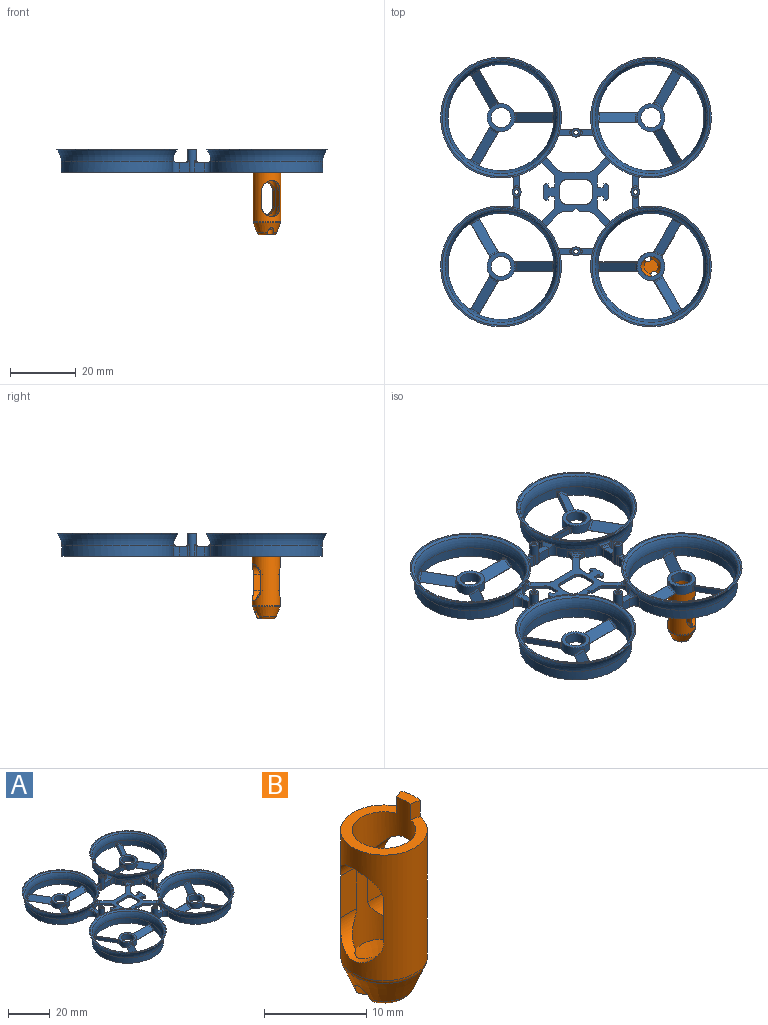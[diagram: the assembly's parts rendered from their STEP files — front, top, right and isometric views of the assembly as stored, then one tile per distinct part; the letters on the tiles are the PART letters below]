
ASSEMBLY  parts=2 mates=1
PART A: 307 faces, bbox 86.5x86.2x9.8 mm
  f0: cylinder r=17mm len=8.72mm, axis (0,0,-1), area 26.2mm2, adj f4,f62,f158,f159,f187,f194,f279
  f1: cylinder r=17mm len=8.72mm, axis (0,0,-1), area 26.2mm2, adj f4,f77,f162,f163,f185,f197,f282
  f2: cylinder r=17mm len=33.99mm, axis (0,0,-1), area 259.6mm2, adj f4,f80,f189,f196
  f3: cylinder r=17mm len=8.72mm, axis (0,0,-1), area 26.2mm2, adj f4,f59,f166,f167,f191,f200,f292
  f4: plane 79.71x79.36mm, normal (0,0,-1), area 1160.2mm2, adj f0,f1,f2,f3,f13,f14,f15,f16
  f5: plane 11.58x7.59mm, normal (0,0,1), area 2.2mm2, adj f33,f35,f43,f74,f229,f230,f257,f258
  f6: plane 12.55x1.9mm, normal (0,0,1), area 2.2mm2, adj f33,f35,f40,f73,f231,f232,f259,f260
  f7: plane 11.25x7.41mm, normal (0,0,1), area 0.3mm2, adj f30,f32,f38,f66,f245,f246,f261,f262
  f8: plane 12.55x1.76mm, normal (0,0,1), area 0.3mm2, adj f30,f32,f48,f68,f241,f242,f267,f268
  f9: plane 12.55x1.76mm, normal (0,0,1), area 0.3mm2, adj f24,f26,f47,f63,f251,f252,f271,f272
  f10: plane 11.25x7.41mm, normal (0,0,1), area 0.3mm2, adj f24,f26,f29,f65,f247,f248,f269,f270
  f11: plane 12.55x1.76mm, normal (0,0,1), area 0.3mm2, adj f21,f23,f45,f71,f235,f236,f253,f254
  f12: plane 11.49x7.48mm, normal (0,0,1), area 0.3mm2, adj f21,f23,f27,f70,f237,f238,f273,f274
  f13: cylinder r=17mm len=33.99mm, axis (0,0,-1), area 259.6mm2, adj f4,f59,f192,f199
  f14: cylinder r=17mm len=33.99mm, axis (0,0,-1), area 259.6mm2, adj f4,f77,f186,f198
  f15: cylinder r=17mm len=8.72mm, axis (0,0,-1), area 26.2mm2, adj f4,f80,f170,f171,f190,f195,f289
  f16: cylinder r=17mm len=33.99mm, axis (0,0,-1), area 259.6mm2, adj f4,f62,f188,f193
  f17: plane 11.49x7.48mm, normal (0,0,1), area 0.3mm2, adj f30,f32,f44,f67,f243,f244,f255,f256
  f18: plane 11.25x7.41mm, normal (0,0,1), area 0.3mm2, adj f24,f26,f36,f64,f249,f250,f263,f264
  f19: plane 11.25x7.41mm, normal (0,0,1), area 0.3mm2, adj f21,f23,f56,f69,f239,f240,f275,f276
  f20: plane 11.31x7.56mm, normal (0,0,1), area 2.2mm2, adj f33,f35,f49,f72,f233,f234,f265,f266
  f21: cylinder r=4.25mm len=8.5mm, axis (0,0,-1), area 64.3mm2, adj f4,f11,f12,f19,f22,f28,f55,f177
  f22: plane 12.26x0.79mm, normal (0,-1,0), area 0.7mm2, adj f4,f21,f23,f71,f235,f236
  f23: cylinder r=16.2mm len=32.39mm, axis (0,0,-1), area 300.6mm2, adj f4,f11,f12,f19,f22,f28,f55,f57
  f24: cylinder r=4.25mm len=8.5mm, axis (0,0,-1), area 64.3mm2, adj f4,f9,f10,f18,f25,f37,f46,f178
  f25: plane 10.64x6.19mm, normal (-0.87,0.5,0), area 0.7mm2, adj f4,f24,f26,f64,f249,f250
  f26: cylinder r=16.2mm len=32.39mm, axis (0,0,-1), area 300.6mm2, adj f4,f9,f10,f18,f25,f37,f46,f75
  f27: plane 9.75x5.63mm, normal (-0.87,-0.5,0), area 22.5mm2, adj f4,f12,f273,f274
  f28: plane 10.64x6.19mm, normal (-0.87,0.5,0), area 0.7mm2, adj f4,f21,f23,f69,f239,f240
  f29: plane 9.75x5.63mm, normal (0.87,0.5,0), area 22.5mm2, adj f4,f10,f269,f270
  f30: cylinder r=4.25mm len=8.5mm, axis (0,0,-1), area 64.3mm2, adj f4,f7,f8,f17,f31,f39,f50,f179
  f31: plane 10.64x6.19mm, normal (-0.87,-0.5,0), area 0.7mm2, adj f4,f30,f32,f67,f243,f244
  f32: cylinder r=16.2mm len=32.39mm, axis (0,0,-1), area 300.6mm2, adj f4,f7,f8,f17,f31,f39,f50,f60
  f33: cylinder r=16.2mm len=32.39mm, axis (0,0,-1), area 300mm2, adj f4,f5,f6,f20,f34,f41,f42,f78
  f34: plane 12.26x0.89mm, normal (0,-1,0), area 2mm2, adj f4,f33,f35,f73,f231,f232
  f35: cylinder r=4.25mm len=8.5mm, axis (0,0,-1), area 63.8mm2, adj f4,f5,f6,f20,f34,f41,f42,f180
  f36: plane 9.75x5.63mm, normal (0.87,-0.5,0), area 22.5mm2, adj f4,f18,f263,f264
  f37: plane 12.26x0.79mm, normal (0,-1,0), area 0.7mm2, adj f4,f24,f26,f63,f251,f252
  f38: plane 9.75x5.63mm, normal (-0.87,0.5,0), area 22.5mm2, adj f4,f7,f261,f262
  f39: plane 12.26x0.79mm, normal (0,1,0), area 0.7mm2, adj f4,f30,f32,f68,f241,f242
  f40: plane 11.26x2mm, normal (0,1,0), area 22.5mm2, adj f4,f6,f259,f260
  f41: plane 10.64x6.19mm, normal (-0.87,0.5,0), area 2mm2, adj f4,f33,f35,f74,f229,f230
  f42: plane 10.64x6.19mm, normal (0.87,0.5,0), area 2mm2, adj f4,f33,f35,f72,f233,f234
  f43: plane 9.75x5.63mm, normal (0.87,-0.5,0), area 22.5mm2, adj f4,f5,f257,f258
  f44: plane 9.75x5.63mm, normal (0.87,0.5,0), area 22.5mm2, adj f4,f17,f255,f256
  f45: plane 11.26x2mm, normal (0,1,0), area 22.5mm2, adj f4,f11,f253,f254
  f46: plane 10.64x6.19mm, normal (-0.87,-0.5,0), area 0.7mm2, adj f4,f24,f26,f65,f247,f248
  f47: plane 11.26x2mm, normal (0,1,0), area 22.5mm2, adj f4,f9,f271,f272
  f48: plane 11.26x2mm, normal (0,-1,0), area 22.5mm2, adj f4,f8,f267,f268
  f49: plane 9.75x5.63mm, normal (-0.87,-0.5,0), area 22.5mm2, adj f4,f20,f265,f266
  f50: plane 10.64x6.19mm, normal (0.87,-0.5,0), area 0.7mm2, adj f4,f30,f32,f66,f245,f246
  f51: cylinder r=3.05mm len=6.1mm, axis (0,0,-1), area 57.5mm2, adj f4,f178
  f52: cylinder r=3.05mm len=6.1mm, axis (0,0,-1), area 57.5mm2, adj f4,f179
  f53: cylinder r=3.05mm len=6.1mm, axis (0,0,-1), area 57.5mm2, adj f4,f180
  f54: cylinder r=3.05mm len=6.1mm, axis (0,0,-1), area 57.5mm2, adj f4,f177
  f55: plane 10.64x6.19mm, normal (0.87,0.5,0), area 0.7mm2, adj f4,f21,f23,f70,f237,f238
  f56: plane 9.75x5.63mm, normal (0.87,-0.5,0), area 22.5mm2, adj f4,f19,f275,f276
  f57: torus R=22.96mm, axis (0,0,1), area 366.2mm2, adj f23,f84
  f58: plane 36.83x36.83mm, normal (0,0,1), area 51.6mm2, adj f59,f84
  f59: torus R=23mm, axis (0,0,1), area 449.2mm2, adj f3,f13,f58,f191,f192,f199,f200,f293
  f60: torus R=22.96mm, axis (0,0,1), area 366.2mm2, adj f32,f83
  f61: plane 36.83x36.83mm, normal (0,0,1), area 51.6mm2, adj f62,f83
  f62: torus R=23mm, axis (0,0,1), area 451.7mm2, adj f0,f16,f61,f187,f188,f193,f194,f214
  f63: plane 11.29x3mm, normal (0,-0.54,0.84), area 39.4mm2, adj f9,f37,f251,f252
  f64: plane 11.23x8.1mm, normal (-0.47,0.27,0.84), area 39.4mm2, adj f18,f25,f249,f250
  f65: plane 11.23x8.1mm, normal (-0.47,-0.27,0.84), area 39.4mm2, adj f10,f46,f247,f248
  f66: plane 11.23x8.1mm, normal (0.47,-0.27,0.84), area 39.4mm2, adj f7,f50,f245,f246
  f67: plane 11.03x8.22mm, normal (-0.47,-0.27,0.84), area 39.4mm2, adj f17,f31,f243,f244
  f68: plane 11.29x3mm, normal (0,0.54,0.84), area 39.4mm2, adj f8,f39,f241,f242
  f69: plane 11.23x8.1mm, normal (-0.47,0.27,0.84), area 39.4mm2, adj f19,f28,f239,f240
  f70: plane 11.03x8.22mm, normal (0.47,0.27,0.84), area 39.4mm2, adj f12,f55,f237,f238
  f71: plane 11.29x3mm, normal (0,-0.54,0.84), area 39.4mm2, adj f11,f22,f235,f236
  f72: plane 11.17x7.95mm, normal (0.47,0.27,0.84), area 37.3mm2, adj f20,f42,f233,f234
  f73: plane 11.29x2.85mm, normal (0,-0.54,0.84), area 37.3mm2, adj f6,f34,f231,f232
  f74: plane 10.92x8.09mm, normal (-0.47,0.27,0.84), area 37.3mm2, adj f5,f41,f229,f230
  f75: torus R=22.96mm, axis (0,0,1), area 366.2mm2, adj f26,f82
  f76: plane 36.83x36.83mm, normal (0,0,1), area 51.6mm2, adj f77,f82
  f77: torus R=23mm, axis (0,0,1), area 451.7mm2, adj f1,f14,f76,f185,f186,f197,f198,f213
  f78: torus R=22.96mm, axis (0,0,1), area 366.2mm2, adj f33,f81
  f79: plane 36.83x36.83mm, normal (0,0,1), area 51.6mm2, adj f80,f81
  f80: torus R=23mm, axis (0,0,1), area 451.7mm2, adj f2,f15,f79,f189,f190,f195,f196,f216
  f81: torus R=17.96mm, axis (0,0,-1), area 115.2mm2, adj f78,f79
  f82: torus R=17.96mm, axis (0,0,-1), area 115.2mm2, adj f75,f76
  f83: torus R=17.96mm, axis (0,0,-1), area 115.2mm2, adj f60,f61
  f84: torus R=17.96mm, axis (0,0,-1), area 115.2mm2, adj f57,f58
  f85: cylinder r=1.35mm len=7mm, axis (0,0,-1), area 40.1mm2, adj f4,f86,f207,f208,f295,f296,f297,f298
  f86: plane 2.7x2.7mm, normal (0,0,1), area 4.4mm2, adj f85,f154
  f87: cylinder r=1.35mm len=7mm, axis (0,0,-1), area 40.1mm2, adj f4,f88,f201,f202,f303,f304,f305,f306
  f88: plane 2.7x2.7mm, normal (0,0,1), area 4.4mm2, adj f87,f153
  f89: cylinder r=1.35mm len=7mm, axis (0,0,-1), area 41.9mm2, adj f4,f90,f107,f109,f203,f204,f299,f300
  f90: plane 2.7x2.7mm, normal (0,0,1), area 4.4mm2, adj f89,f156
  f91: cylinder r=1.35mm len=7mm, axis (0,0,-1), area 41.9mm2, adj f4,f92,f101,f103,f205,f206,f301,f302
  f92: plane 2.7x2.7mm, normal (0,0,1), area 4.4mm2, adj f91,f155
  f93: plane 4.21x2.44mm, normal (0,0,1), area 7.6mm2, adj f94,f95,f187,f188,f208,f214
  f94: plane 3.08x2.71mm, normal (0,1,0), area 8.1mm2, adj f4,f93,f188,f208,f298
  f95: plane 4.22x3.08mm, normal (0,-1,0), area 12.6mm2, adj f4,f93,f187,f208,f296
  f96: plane 4.21x2.44mm, normal (0,0,1), area 7.6mm2, adj f97,f98,f185,f186,f207,f213
  f97: plane 3.08x2.71mm, normal (0,1,0), area 8.1mm2, adj f4,f96,f186,f207,f297
  f98: plane 4.22x3.08mm, normal (0,-1,0), area 12.6mm2, adj f4,f96,f185,f207,f295
  f99: plane 4.09x2.45mm, normal (0,0,1), area 7.4mm2, adj f100,f101,f195,f196,f206,f216
  f100: plane 4.13x3.08mm, normal (-1,0,0), area 12.4mm2, adj f4,f99,f195,f206,f302
  f101: plane 3.59x2.96mm, normal (1,0,0), area 8.7mm2, adj f4,f91,f99,f196,f206
  f102: plane 3.65x2.19mm, normal (0,0,1), area 6.4mm2, adj f103,f104,f193,f205,f278
  f103: plane 3.59x2.96mm, normal (1,0,0), area 8.7mm2, adj f4,f91,f102,f193,f205
  f104: plane 4.13x3.08mm, normal (-1,0,0), area 12.4mm2, adj f4,f102,f194,f205,f278,f301
  f105: plane 3.76x2.18mm, normal (0,0,1), area 6.6mm2, adj f106,f107,f189,f204,f288
  f106: plane 4.22x3.08mm, normal (0,1,0), area 12.6mm2, adj f4,f105,f190,f204,f288,f299
  f107: plane 3.59x3.12mm, normal (0,-1,0), area 9.1mm2, adj f4,f89,f105,f189,f204
  f108: plane 3.76x2.18mm, normal (0,0,1), area 6.6mm2, adj f109,f110,f192,f203,f291
  f109: plane 3.59x3.12mm, normal (0,-1,0), area 9.1mm2, adj f4,f89,f108,f192,f203
  f110: plane 4.22x3.08mm, normal (0,1,0), area 12.6mm2, adj f4,f108,f191,f203,f291,f300
  f111: plane 3.65x2.19mm, normal (0,0,1), area 6.4mm2, adj f112,f113,f199,f202,f283
  f112: plane 3.08x2.55mm, normal (-1,0,0), area 7.6mm2, adj f4,f111,f199,f202,f306
  f113: plane 4.13x3.08mm, normal (1,0,0), area 12.4mm2, adj f4,f111,f200,f202,f283,f303
  f114: plane 3.65x2.19mm, normal (0,0,1), area 6.4mm2, adj f115,f116,f198,f201,f277
  f115: plane 4.13x3.08mm, normal (1,0,0), area 12.4mm2, adj f4,f114,f197,f201,f277,f304
  f116: plane 3.08x2.55mm, normal (-1,0,0), area 7.6mm2, adj f4,f114,f198,f201,f305
  f117: plane 5.8x1mm, normal (0,-1,0), area 5.8mm2, adj f4,f152,f173,f176
  f118: plane 3.5x1mm, normal (-1,0,0), area 3.5mm2, adj f4,f152,f173,f174
  f119: plane 5.8x1mm, normal (0,1,0), area 5.8mm2, adj f4,f152,f174,f175
  f120: plane 2.41x1mm, normal (1,0,0), area 2.4mm2, adj f4,f152,f157,f228
  f121: plane 3.21x3.19mm, normal (0.7,-0.71,0), area 4.5mm2, adj f4,f152,f157,f158
  f122: plane 3.63x3.6mm, normal (-0.7,0.71,0), area 5.1mm2, adj f4,f152,f159,f160
  f123: plane 7.6x1mm, normal (0,1,0), area 7.6mm2, adj f4,f152,f160,f161
  f124: plane 3.63x3.6mm, normal (0.7,0.71,0), area 5.1mm2, adj f4,f152,f161,f162
  f125: plane 3.21x3.19mm, normal (-0.7,-0.71,0), area 4.5mm2, adj f4,f152,f163,f164
  f126: plane 2.41x1mm, normal (-1,0,0), area 2.4mm2, adj f4,f152,f164,f221
  f127: plane 1x1mm, normal (0,1,0), area 1mm2, adj f4,f152,f221,f222
  f128: plane 1x0.75mm, normal (1,0,0), area 0.8mm2, adj f4,f129,f152,f222
  f129: plane 1x0.5mm, normal (0,1,0), area 0.5mm2, adj f4,f128,f152,f181
  f130: plane 3x1mm, normal (-1,0,0), area 3mm2, adj f4,f152,f181,f182
  f131: plane 1x0.5mm, normal (0,-1,0), area 0.5mm2, adj f4,f132,f152,f182
  f132: plane 1x0.75mm, normal (1,0,0), area 0.8mm2, adj f4,f131,f152,f223
  f133: plane 1x1mm, normal (0,-1,0), area 1mm2, adj f4,f152,f223,f224
  f134: plane 2.41x1mm, normal (-1,0,0), area 2.4mm2, adj f4,f152,f165,f224
  f135: plane 3.21x3.19mm, normal (-0.7,0.71,0), area 4.5mm2, adj f4,f152,f165,f166
  f136: plane 3.63x3.6mm, normal (0.7,-0.71,0), area 5.1mm2, adj f4,f152,f167,f168
  f137: plane 2.81x1mm, normal (0,-1,0), area 2.8mm2, adj f4,f138,f152,f168
  f138: plane 1x1mm, normal (0.71,-0.7,0), area 1.4mm2, adj f4,f137,f139,f152
  f139: plane 1.01x1mm, normal (-0.7,-0.71,0), area 1.4mm2, adj f4,f138,f140,f152
  f140: plane 2.79x1mm, normal (0,-1,0), area 2.8mm2, adj f4,f139,f152,f169
  f141: plane 3.63x3.6mm, normal (-0.7,-0.71,0), area 5.1mm2, adj f4,f152,f169,f170
  f142: plane 3.21x3.19mm, normal (0.7,0.71,0), area 4.5mm2, adj f4,f152,f171,f172
  f143: plane 2.41x1mm, normal (1,0,0), area 2.4mm2, adj f4,f152,f172,f225
  f144: plane 1x1mm, normal (0,-1,0), area 1mm2, adj f4,f152,f225,f226
  f145: plane 1x0.75mm, normal (-1,0,0), area 0.8mm2, adj f4,f146,f152,f226
  f146: plane 1x0.5mm, normal (0,-1,0), area 0.5mm2, adj f4,f145,f152,f183
  f147: plane 3x1mm, normal (1,0,0), area 3mm2, adj f4,f152,f183,f184
  f148: plane 1x0.5mm, normal (0,1,0), area 0.5mm2, adj f4,f149,f152,f184
  f149: plane 1x0.75mm, normal (-1,0,0), area 0.8mm2, adj f4,f148,f152,f227
  f150: plane 1x1mm, normal (0,1,0), area 1mm2, adj f4,f152,f227,f228
  f151: plane 3.5x1mm, normal (1,0,0), area 3.5mm2, adj f4,f152,f175,f176
  f152: plane 21.09x20.95mm, normal (0,0,1), area 153.4mm2, adj f117,f118,f119,f120,f121,f122,f123,f124
  f153: cylinder r=0.65mm len=7mm, axis (0,0,1), area 28.6mm2, adj f4,f88
  f154: cylinder r=0.65mm len=7mm, axis (0,0,1), area 28.6mm2, adj f4,f86
  f155: cylinder r=0.65mm len=7mm, axis (0,0,1), area 28.6mm2, adj f4,f92
  f156: cylinder r=0.65mm len=7mm, axis (0,0,1), area 28.6mm2, adj f4,f90
  f157: cylinder r=2mm len=1.42mm, axis (0,0,-1), area 1.6mm2, adj f4,f120,f121,f152
  f158: cylinder r=2mm len=2.59mm, axis (0,0,-1), area 4.4mm2, adj f0,f4,f121,f152,f220,f279,f287
  f159: cylinder r=2mm len=2.59mm, axis (0,0,-1), area 4.4mm2, adj f0,f4,f122,f152,f220,f279,f287
  f160: cylinder r=2mm len=1.41mm, axis (0,0,1), area 1.6mm2, adj f4,f122,f123,f152
  f161: cylinder r=2mm len=1.41mm, axis (0,0,1), area 1.6mm2, adj f4,f123,f124,f152
  f162: cylinder r=2mm len=2.59mm, axis (0,0,-1), area 4.4mm2, adj f1,f4,f124,f152,f219,f282,f286
  f163: cylinder r=2mm len=2.59mm, axis (0,0,-1), area 4.4mm2, adj f1,f4,f125,f152,f219,f282,f286
  f164: cylinder r=2mm len=1.42mm, axis (0,0,1), area 1.6mm2, adj f4,f125,f126,f152
  f165: cylinder r=2mm len=1.42mm, axis (0,0,-1), area 1.6mm2, adj f4,f134,f135,f152
  f166: cylinder r=2mm len=2.59mm, axis (0,0,-1), area 4.4mm2, adj f3,f4,f135,f152,f215,f285,f292
  f167: cylinder r=2mm len=2.59mm, axis (0,0,-1), area 4.4mm2, adj f3,f4,f136,f152,f215,f285,f292
  f168: cylinder r=2mm len=1.41mm, axis (0,0,1), area 1.6mm2, adj f4,f136,f137,f152
  f169: cylinder r=2mm len=1.41mm, axis (0,0,1), area 1.6mm2, adj f4,f140,f141,f152
  f170: cylinder r=2mm len=2.59mm, axis (0,0,-1), area 4.4mm2, adj f4,f15,f141,f152,f211,f284,f289
  f171: cylinder r=2mm len=2.59mm, axis (0,0,-1), area 4.4mm2, adj f4,f15,f142,f152,f211,f284,f289
  f172: cylinder r=2mm len=1.42mm, axis (0,0,1), area 1.6mm2, adj f4,f142,f143,f152
  f173: cylinder r=2mm len=2mm, axis (0,0,1), area 3.1mm2, adj f4,f117,f118,f152
  f174: cylinder r=2mm len=2mm, axis (0,0,-1), area 3.1mm2, adj f4,f118,f119,f152
  f175: cylinder r=2mm len=2mm, axis (0,0,1), area 3.1mm2, adj f4,f119,f151,f152
  f176: cylinder r=2mm len=2mm, axis (0,0,-1), area 3.1mm2, adj f4,f117,f151,f152
  f177: plane 8.5x8.5mm, normal (0,0,1), area 27.5mm2, adj f21,f54
  f178: plane 8.5x8.5mm, normal (0,0,1), area 27.5mm2, adj f24,f51
  f179: plane 8.5x8.5mm, normal (0,0,1), area 27.5mm2, adj f30,f52
  f180: plane 8.5x8.5mm, normal (0,0,1), area 27.5mm2, adj f35,f53
  f181: cylinder r=1mm len=1mm, axis (0,0,-1), area 1.6mm2, adj f4,f129,f130,f152
  f182: cylinder r=1mm len=1mm, axis (0,0,-1), area 1.6mm2, adj f4,f130,f131,f152
  f183: cylinder r=1mm len=1mm, axis (0,0,-1), area 1.6mm2, adj f4,f146,f147,f152
  f184: cylinder r=1mm len=1mm, axis (0,0,-1), area 1.6mm2, adj f4,f147,f148,f152
  f185: cylinder r=2mm len=3.94mm, axis (0,0,-1), area 7.9mm2, adj f1,f4,f77,f96,f98,f213
  f186: cylinder r=2mm len=3.94mm, axis (0,0,-1), area 10.9mm2, adj f4,f14,f77,f96,f97,f213
  f187: cylinder r=2mm len=3.94mm, axis (0,0,-1), area 7.9mm2, adj f0,f4,f62,f93,f95,f214
  f188: cylinder r=2mm len=3.94mm, axis (0,0,-1), area 10.9mm2, adj f4,f16,f62,f93,f94,f214
  f189: cylinder r=2mm len=4.51mm, axis (0,0,-1), area 11.2mm2, adj f2,f4,f80,f105,f107,f210,f288,f290
  f190: cylinder r=2mm len=4.51mm, axis (0,0,-1), area 8.2mm2, adj f4,f15,f80,f106,f210,f288,f290
  f191: cylinder r=2mm len=4.51mm, axis (0,0,-1), area 8.2mm2, adj f3,f4,f59,f110,f209,f291,f293
  f192: cylinder r=2mm len=4.51mm, axis (0,0,-1), area 11.2mm2, adj f4,f13,f59,f108,f109,f209,f291,f293
  f193: cylinder r=2mm len=4.51mm, axis (0,0,-1), area 11.3mm2, adj f4,f16,f62,f102,f103,f217,f278,f280
  f194: cylinder r=2mm len=4.51mm, axis (0,0,-1), area 8.2mm2, adj f0,f4,f62,f104,f217,f278,f280
  f195: cylinder r=2mm len=3.94mm, axis (0,0,-1), area 7.9mm2, adj f4,f15,f80,f99,f100,f216
  f196: cylinder r=2mm len=3.94mm, axis (0,0,-1), area 11mm2, adj f2,f4,f80,f99,f101,f216
  f197: cylinder r=2mm len=4.51mm, axis (0,0,-1), area 8.2mm2, adj f1,f4,f77,f115,f218,f277,f281
  f198: cylinder r=2mm len=4.51mm, axis (0,0,-1), area 11.3mm2, adj f4,f14,f77,f114,f116,f218,f277,f281
  f199: cylinder r=2mm len=4.51mm, axis (0,0,-1), area 11.3mm2, adj f4,f13,f59,f111,f112,f212,f283,f294
  f200: cylinder r=2mm len=4.51mm, axis (0,0,-1), area 8.2mm2, adj f3,f4,f59,f113,f212,f283,f294
  f201: torus R=1.85mm, axis (0,0,1), area 1.8mm2, adj f87,f114,f115,f116,f304,f305
  f202: torus R=1.85mm, axis (0,0,1), area 1.8mm2, adj f87,f111,f112,f113,f303,f306
  f203: torus R=1.85mm, axis (0,0,1), area 1.7mm2, adj f89,f108,f109,f110,f300
  f204: torus R=1.85mm, axis (0,0,1), area 1.7mm2, adj f89,f105,f106,f107,f299
  f205: torus R=1.85mm, axis (0,0,1), area 1.7mm2, adj f91,f102,f103,f104,f301
  f206: torus R=1.85mm, axis (0,0,1), area 1.7mm2, adj f91,f99,f100,f101,f302
  f207: torus R=1.85mm, axis (0,0,1), area 1.8mm2, adj f85,f96,f97,f98,f295,f297
  f208: torus R=1.85mm, axis (0,0,1), area 1.8mm2, adj f85,f93,f94,f95,f296,f298
  f209: cone r=17mm half-angle=45deg, axis (0,0,-1), area 1.2mm2, adj f191,f192,f291,f293
  f210: cone r=17mm half-angle=45deg, axis (0,0,-1), area 1.2mm2, adj f189,f190,f288,f290
  f211: cone r=17mm half-angle=45deg, axis (0,0,-1), area 1.8mm2, adj f170,f171,f284,f289
  f212: cone r=17mm half-angle=45deg, axis (0,0,-1), area 1.2mm2, adj f199,f200,f283,f294
  f213: cone r=18mm half-angle=45deg, axis (0,0,-1), area 4.8mm2, adj f77,f96,f185,f186
  f214: cone r=17mm half-angle=45deg, axis (0,0,-1), area 4.8mm2, adj f62,f93,f187,f188
  f215: cone r=17mm half-angle=45deg, axis (0,0,-1), area 1.8mm2, adj f166,f167,f285,f292
  f216: cone r=17mm half-angle=45deg, axis (0,0,-1), area 4.9mm2, adj f80,f99,f195,f196
  f217: cone r=17mm half-angle=45deg, axis (0,0,-1), area 1.2mm2, adj f193,f194,f278,f280
  f218: cone r=17mm half-angle=45deg, axis (0,0,-1), area 1.2mm2, adj f197,f198,f277,f281
  f219: cone r=17mm half-angle=45deg, axis (0,0,-1), area 1.8mm2, adj f162,f163,f282,f286
  f220: cone r=17mm half-angle=45deg, axis (0,0,-1), area 1.8mm2, adj f158,f159,f279,f287
  f221: cylinder r=0.5mm len=1mm, axis (0,0,1), area 0.8mm2, adj f4,f126,f127,f152
  f222: cylinder r=0.5mm len=1mm, axis (0,0,1), area 0.8mm2, adj f4,f127,f128,f152
  f223: cylinder r=0.5mm len=1mm, axis (0,0,1), area 0.8mm2, adj f4,f132,f133,f152
  f224: cylinder r=0.5mm len=1mm, axis (0,0,1), area 0.8mm2, adj f4,f133,f134,f152
  f225: cylinder r=0.5mm len=1mm, axis (0,0,1), area 0.8mm2, adj f4,f143,f144,f152
  f226: cylinder r=0.5mm len=1mm, axis (0,0,1), area 0.8mm2, adj f4,f144,f145,f152
  f227: cylinder r=0.5mm len=1mm, axis (0,0,-1), area 0.8mm2, adj f4,f149,f150,f152
  f228: cylinder r=0.5mm len=1mm, axis (0,0,-1), area 0.8mm2, adj f4,f120,f150,f152
  f229: bspline ~2.92x2.29mm, area 2.3mm2, adj f5,f35,f41,f74
  f230: bspline ~5.06x4mm, area 2.3mm2, adj f5,f33,f41,f74
  f231: bspline ~3.17x2.27mm, area 2.3mm2, adj f6,f33,f34,f73
  f232: bspline ~2.97x2.29mm, area 2.3mm2, adj f6,f34,f35,f73
  f233: bspline ~2.44x2.29mm, area 2.3mm2, adj f20,f35,f42,f72
  f234: bspline ~5.28x4mm, area 2.3mm2, adj f20,f33,f42,f72
  f235: bspline ~3.12x2.39mm, area 2.5mm2, adj f11,f21,f22,f71
  f236: bspline ~5.87x4mm, area 2.4mm2, adj f11,f22,f23,f71
  f237: bspline ~3.03x2.39mm, area 2.5mm2, adj f12,f21,f55,f70
  f238: bspline ~5.06x4mm, area 2.4mm2, adj f12,f23,f55,f70
  f239: bspline ~3.61x3.03mm, area 2.5mm2, adj f19,f21,f28,f69
  f240: bspline ~5.28x4mm, area 2.4mm2, adj f19,f23,f28,f69
  f241: bspline ~3.33x2.37mm, area 2.4mm2, adj f8,f32,f39,f68
  f242: bspline ~3.12x2.39mm, area 2.5mm2, adj f8,f30,f39,f68
  f243: bspline ~3.03x2.39mm, area 2.5mm2, adj f17,f30,f31,f67
  f244: bspline ~5.06x4mm, area 2.4mm2, adj f17,f31,f32,f67
  f245: bspline ~3.61x3.03mm, area 2.5mm2, adj f7,f30,f50,f66
  f246: bspline ~5.28x4mm, area 2.4mm2, adj f7,f32,f50,f66
  f247: bspline ~3.61x3.03mm, area 2.5mm2, adj f10,f24,f46,f65
  f248: bspline ~5.28x4mm, area 2.4mm2, adj f10,f26,f46,f65
  f249: bspline ~3.61x3.03mm, area 2.5mm2, adj f18,f24,f25,f64
  f250: bspline ~5.28x4mm, area 2.4mm2, adj f18,f25,f26,f64
  f251: bspline ~3.12x2.39mm, area 2.5mm2, adj f9,f24,f37,f63
  f252: bspline ~5.87x4mm, area 2.4mm2, adj f9,f26,f37,f63
  f253: cylinder r=0.5mm len=2mm, axis (0,0,-1), area 1.7mm2, adj f4,f11,f23,f45
  f254: cylinder r=0.5mm len=2mm, axis (0,0,-1), area 1.1mm2, adj f4,f11,f21,f45
  f255: cylinder r=0.5mm len=2mm, axis (0,0,-1), area 1.7mm2, adj f4,f17,f32,f44
  f256: cylinder r=0.5mm len=2mm, axis (0,0,-1), area 1.1mm2, adj f4,f17,f30,f44
  f257: cylinder r=0.5mm len=2mm, axis (0,0,-1), area 1.1mm2, adj f4,f5,f35,f43
  f258: cylinder r=0.5mm len=2mm, axis (0,0,-1), area 1.7mm2, adj f4,f5,f33,f43
  f259: cylinder r=0.5mm len=2mm, axis (0,0,-1), area 1.7mm2, adj f4,f6,f33,f40
  f260: cylinder r=0.5mm len=2mm, axis (0,0,-1), area 1.1mm2, adj f4,f6,f35,f40
  f261: cylinder r=0.5mm len=2mm, axis (0,0,-1), area 1.1mm2, adj f4,f7,f30,f38
  f262: cylinder r=0.5mm len=2mm, axis (0,0,-1), area 1.7mm2, adj f4,f7,f32,f38
  f263: cylinder r=0.5mm len=2mm, axis (0,0,-1), area 1.1mm2, adj f4,f18,f24,f36
  f264: cylinder r=0.5mm len=2mm, axis (0,0,-1), area 1.7mm2, adj f4,f18,f26,f36
  f265: cylinder r=0.5mm len=2mm, axis (0,0,-1), area 1.1mm2, adj f4,f20,f35,f49
  f266: cylinder r=0.5mm len=2mm, axis (0,0,-1), area 1.7mm2, adj f4,f20,f33,f49
  f267: cylinder r=0.5mm len=2mm, axis (0,0,-1), area 1.7mm2, adj f4,f8,f32,f48
  f268: cylinder r=0.5mm len=2mm, axis (0,0,-1), area 1.1mm2, adj f4,f8,f30,f48
  f269: cylinder r=0.5mm len=2mm, axis (0,0,-1), area 1.1mm2, adj f4,f10,f24,f29
  f270: cylinder r=0.5mm len=2mm, axis (0,0,-1), area 1.7mm2, adj f4,f10,f26,f29
  f271: cylinder r=0.5mm len=2mm, axis (0,0,-1), area 1.7mm2, adj f4,f9,f26,f47
  f272: cylinder r=0.5mm len=2mm, axis (0,0,-1), area 1.1mm2, adj f4,f9,f24,f47
  f273: cylinder r=0.5mm len=2mm, axis (0,0,-1), area 1.1mm2, adj f4,f12,f21,f27
  f274: cylinder r=0.5mm len=2mm, axis (0,0,-1), area 1.7mm2, adj f4,f12,f23,f27
  f275: cylinder r=0.5mm len=2mm, axis (0,0,-1), area 1.7mm2, adj f4,f19,f23,f56
  f276: cylinder r=0.5mm len=2mm, axis (0,0,-1), area 1.1mm2, adj f4,f19,f21,f56
  f277: torus R=18.41mm, axis (0,0,1), area 2mm2, adj f114,f115,f197,f198,f218
  f278: torus R=18.41mm, axis (0,0,1), area 2mm2, adj f102,f104,f193,f194,f217
  f279: torus R=18mm, axis (0,0,1), area 3.5mm2, adj f0,f158,f159,f220
  f280: torus R=18.13mm, axis (0,0,1), area 4mm2, adj f62,f193,f194,f217
  f281: torus R=18.13mm, axis (0,0,1), area 4mm2, adj f77,f197,f198,f218
  f282: torus R=18mm, axis (0,0,1), area 3.5mm2, adj f1,f162,f163,f219
  f283: torus R=18.41mm, axis (0,0,1), area 2mm2, adj f111,f113,f199,f200,f212
  f284: torus R=18.41mm, axis (0,0,1), area 1.9mm2, adj f152,f170,f171,f211
  f285: torus R=18.41mm, axis (0,0,1), area 1.9mm2, adj f152,f166,f167,f215
  f286: torus R=18.41mm, axis (0,0,1), area 1.9mm2, adj f152,f162,f163,f219
  f287: torus R=18.41mm, axis (0,0,1), area 1.9mm2, adj f152,f158,f159,f220
  f288: torus R=18.41mm, axis (0,0,1), area 2mm2, adj f105,f106,f189,f190,f210
  f289: torus R=18mm, axis (0,0,1), area 3.5mm2, adj f15,f170,f171,f211
  f290: torus R=18.13mm, axis (0,0,1), area 4mm2, adj f80,f189,f190,f210
  f291: torus R=18.41mm, axis (0,0,1), area 2mm2, adj f108,f110,f191,f192,f209
  f292: torus R=18mm, axis (0,0,1), area 3.5mm2, adj f3,f166,f167,f215
  f293: torus R=18.13mm, axis (0,0,1), area 4mm2, adj f59,f191,f192,f209
  f294: torus R=18.13mm, axis (0,0,1), area 4mm2, adj f59,f199,f200,f212
  f295: cylinder r=1mm len=3.5mm, axis (0,0,-1), area 1.8mm2, adj f4,f85,f98,f207
  f296: cylinder r=1mm len=3.5mm, axis (0,0,-1), area 1.8mm2, adj f4,f85,f95,f208
  f297: cylinder r=1mm len=3.5mm, axis (0,0,-1), area 1.8mm2, adj f4,f85,f97,f207
  f298: cylinder r=1mm len=3.5mm, axis (0,0,-1), area 1.8mm2, adj f4,f85,f94,f208
  f299: cylinder r=1mm len=3.5mm, axis (0,0,-1), area 1.8mm2, adj f4,f89,f106,f204
  f300: cylinder r=1mm len=3.5mm, axis (0,0,-1), area 1.8mm2, adj f4,f89,f110,f203
  f301: cylinder r=1mm len=3.5mm, axis (0,0,-1), area 1.8mm2, adj f4,f91,f104,f205
  f302: cylinder r=1mm len=3.5mm, axis (0,0,-1), area 1.8mm2, adj f4,f91,f100,f206
  f303: cylinder r=1mm len=3.5mm, axis (0,0,-1), area 1.8mm2, adj f4,f87,f113,f202
  f304: cylinder r=1mm len=3.5mm, axis (0,0,-1), area 1.8mm2, adj f4,f87,f115,f201
  f305: cylinder r=1mm len=3.5mm, axis (0,0,-1), area 1.8mm2, adj f4,f87,f116,f201
  f306: cylinder r=1mm len=3.5mm, axis (0,0,-1), area 1.8mm2, adj f4,f87,f112,f202
PART B: 24 faces, bbox 9.2x9.2x21 mm
  f0: plane 8.5x8.41mm, normal (0,0,1), area 24mm2, adj f3,f4,f21,f22
  f1: cone r=3.1mm half-angle=22deg, axis (0,0,1), area 15.8mm2, adj f3,f13,f14,f15
  f2: torus R=2.04mm, axis (0,0,-1), area 7.3mm2, adj f13,f14,f17,f18
  f3: cylinder r=3.1mm len=17.14mm, axis (0,0,-1), area 143.1mm2, adj f0,f1,f5,f6,f7,f8,f9,f10
  f4: cylinder r=4.25mm len=16.95mm, axis (0,0,-1), area 279mm2, adj f0,f5,f6,f7,f8,f9,f10,f11
  f5: cylinder r=3mm len=6mm, axis (1,0,0), area 14.5mm2, adj f3,f4,f6,f8
  f6: plane 5x2.23mm, normal (0,-1,0), area 11.1mm2, adj f3,f4,f5,f7
  f7: cylinder r=3mm len=6mm, axis (1,0,0), area 13.8mm2, adj f3,f4,f6,f8,f14
  f8: plane 5x2.23mm, normal (0,1,0), area 11.1mm2, adj f3,f4,f5,f7
  f9: plane 5x2.23mm, normal (0,1,0), area 11.1mm2, adj f3,f4,f10,f12
  f10: cylinder r=3mm len=6mm, axis (1,0,0), area 13.8mm2, adj f3,f4,f9,f11,f13
  f11: plane 5x2.23mm, normal (0,-1,0), area 11.1mm2, adj f3,f4,f10,f12
  f12: cylinder r=3mm len=6mm, axis (1,0,0), area 14.5mm2, adj f3,f4,f9,f11
  f13: cylinder r=1mm len=5.7mm, axis (0,0,-1), area 16.7mm2, adj f1,f2,f3,f10,f15,f16,f17,f18
  f14: cylinder r=1mm len=5.7mm, axis (0,0,-1), area 16.7mm2, adj f1,f2,f3,f7,f15,f16,f17,f18
  f15: plane 4.33x4.02mm, normal (0,0,1), area 13.5mm2, adj f1,f13,f14,f16
  f16: cone r=3.1mm half-angle=22deg, axis (0,0,1), area 15.8mm2, adj f3,f13,f14,f15
  f17: plane 4.07x3.81mm, normal (0,0,-1), area 12.2mm2, adj f2,f13,f14,f20
  f18: cone r=2.71mm half-angle=22deg, axis (0,0,1), area 67.6mm2, adj f2,f13,f14,f19,f20
  f19: torus R=3.25mm, axis (0,0,-1), area 10.2mm2, adj f4,f18
  f20: torus R=2.04mm, axis (0,0,-1), area 7.3mm2, adj f13,f14,f17,f18
  f21: plane 1.9x1.13mm, normal (-0.2,-0.98,0), area 2.2mm2, adj f0,f3,f4,f23
  f22: plane 1.9x1.06mm, normal (-0.38,0.92,0), area 2.2mm2, adj f0,f3,f4,f23
  f23: plane 2.47x1.39mm, normal (0,0,1), area 2.5mm2, adj f3,f4,f21,f22
PLACE A t=(10.27,0.72,-13.19)mm fixed
PLACE B rot(axis=(0,0,1),112.2deg) t=(33.13,-21.96,-28.46)mm
MATE revolute B.f1 <-> A.f2  axis (0,0,-1) through (33.13,-21.96,-19.79)mm
